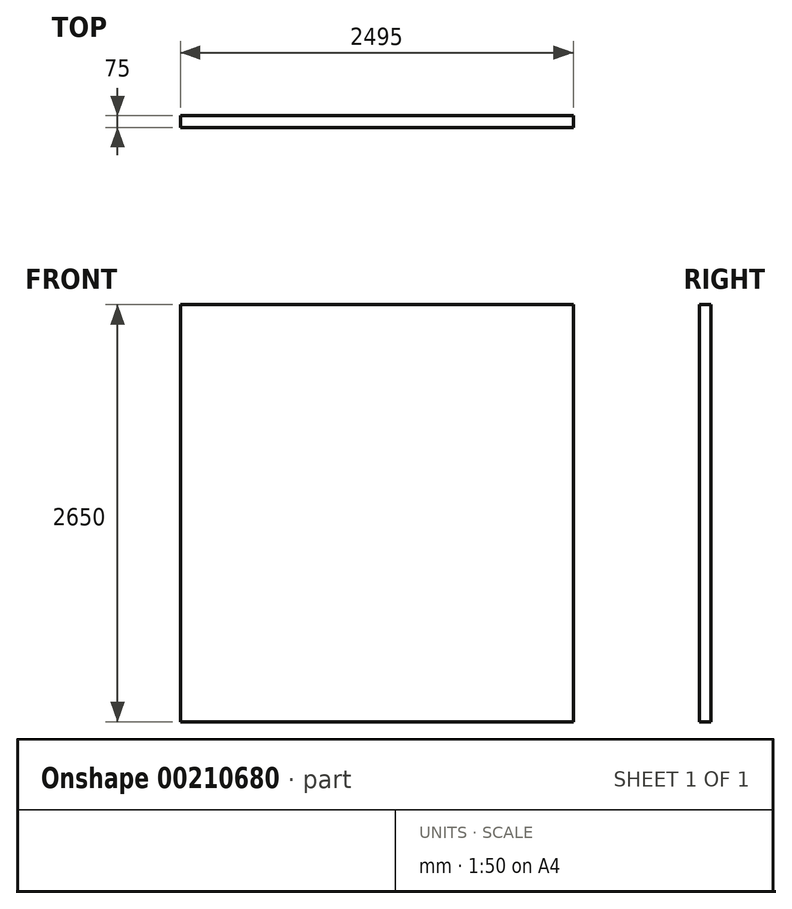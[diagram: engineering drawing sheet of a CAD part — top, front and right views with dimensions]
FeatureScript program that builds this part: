
annotation { "Feature Type Name" : "Feature", "Feature Type Description" : "" }
export const myFeature = defineFeature(function(context is Context, id is Id, definition is map)
    precondition{}
    {
        {
            var Q0;
            Q0=qCreatedBy(makeId("Front.planeOp"),FACE);
            var sketch = newSketch(context, id + "F0", { "sketchPlane" : qUnion([Q0])});
            skLineSegment(sketch, "E0.bottom", {"start": v(0, 0) * mm, "end": v(2495, 0) * mm});
            skLineSegment(sketch, "E0.left", {"start": v(0, 0) * mm, "end": v(0, 2650) * mm});
            skLineSegment(sketch, "E0.right", {"start": v(2495, 0) * mm, "end": v(2495, 2650) * mm});
            skLineSegment(sketch, "E1", {"start": v(0, 2650) * mm, "end": v(2495, 2650) * mm});
            skSolve(sketch);
        }
        {
            var Q0;
            Q0=makeQuery(id+"F0.imprint","IMPRINT",FACE,{"disambiguationData":[TD([[makeQuery(id+"F0.imprint","IMPRINT",EDGE,{"derivedFrom":sQuery(id+"F0.wireOp",EDGE,"E0.bottom")}),1.0]])]});
            extrude(context, id + "F1", {"entities" : qUnion([Q0]), "depth" : 75 * mm});
        }
    });
